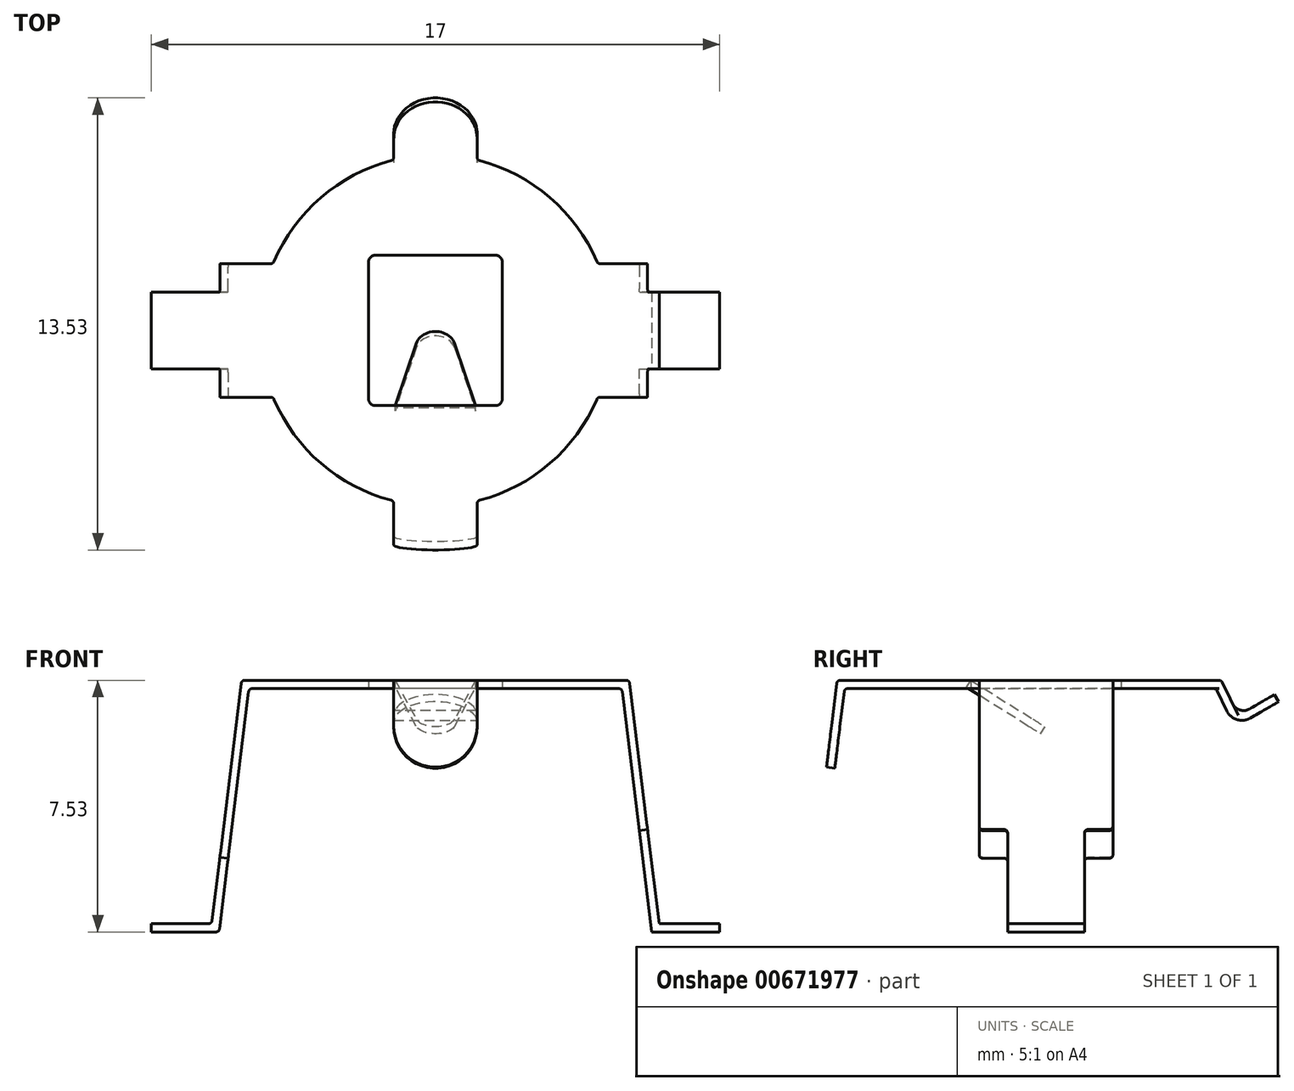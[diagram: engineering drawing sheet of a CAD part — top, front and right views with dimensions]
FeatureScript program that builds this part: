
annotation { "Feature Type Name" : "Feature", "Feature Type Description" : "" }
export const myFeature = defineFeature(function(context is Context, id is Id, definition is map)
    precondition{}
    {
        {
            var Q0;
            Q0=qCreatedBy(makeId("Top.planeOp"),FACE);
            var sketch = newSketch(context, id + "F0", { "sketchPlane" : qUnion([Q0])});
            skArc(sketch, "E0", {"start": v(-1.25, 5.1) * mm, "mid": v(-3.42, 3.98) * mm, "end": v(-4.85, 2) * mm});
            skLineSegment(sketch, "E1", {"start": v(-1.25, 5.24) * mm, "end": v(-1.25, 5.1) * mm});
            skLineSegment(sketch, "E2", {"start": v(1.25, 5.1) * mm, "end": v(1.25, 5.24) * mm});
            skLineSegment(sketch, "E3", {"start": v(-1.25, -5.1) * mm, "end": v(-1.25, -6.25) * mm});
            skLineSegment(sketch, "E4", {"start": v(-1.25, -6.25) * mm, "end": v(1.25, -6.25) * mm});
            skLineSegment(sketch, "E5", {"start": v(1.25, -6.25) * mm, "end": v(1.25, -5.1) * mm});
            skArc(sketch, "E6.trimOffspring", {"start": v(1.25, -5.1) * mm, "mid": v(3.42, -3.98) * mm, "end": v(4.85, -2) * mm});
            skPoint(sketch, "E7.end.orphan", {"position": v(0, -6.25) * mm});
            skArc(sketch, "E8.trimOffspring", {"start": v(-4.85, -2) * mm, "mid": v(-3.42, -3.98) * mm, "end": v(-1.25, -5.1) * mm});
            skArc(sketch, "E9.trimOffspring", {"start": v(4.85, 2) * mm, "mid": v(3.42, 3.98) * mm, "end": v(1.25, 5.1) * mm});
            skLineSegment(sketch, "E10", {"start": v(-5.8, 2) * mm, "end": v(-4.85, 2) * mm});
            skLineSegment(sketch, "E11", {"start": v(-5.8, 2) * mm, "end": v(-5.8, -2) * mm});
            skLineSegment(sketch, "E12", {"start": v(-5.8, -2) * mm, "end": v(-4.85, -2) * mm});
            skLineSegment(sketch, "E13", {"start": v(5.8, 2) * mm, "end": v(4.85, 2) * mm});
            skLineSegment(sketch, "E14", {"start": v(5.8, -2) * mm, "end": v(4.85, -2) * mm});
            skLineSegment(sketch, "E15", {"start": v(5.8, -2) * mm, "end": v(5.8, 2) * mm});
            skLineSegment(sketch, "E16", {"start": v(-1.25, 5.24) * mm, "end": v(1.25, 5.24) * mm});
            skLineSegment(sketch, "E17.bottom", {"start": v(2, -2.25) * mm, "end": v(-2, -2.25) * mm});
            skLineSegment(sketch, "E17.top", {"start": v(2, 2.25) * mm, "end": v(-2, 2.25) * mm});
            skLineSegment(sketch, "E17.left", {"start": v(2, -2.25) * mm, "end": v(2, 2.25) * mm});
            skLineSegment(sketch, "E17.right", {"start": v(-2, -2.25) * mm, "end": v(-2, 2.25) * mm});
            skSolve(sketch);
        }
        {
            var Q0;
            Q0 = qSketchRegion(id + "F0", true);
            extrude(context, id + "F1", {"entities" : qUnion([Q0]), "depth" : 0.25 * mm, "offsetDistance" : 25 * mm});
        }
        {
            var Q0;
            Q0=makeQuery(id+"F1.opExtrude","SWEPT_FACE",FACE,{"disambiguationData":[OSD([sQuery(id+"F0.wireOp",EDGE,"E12")])]});
            var sketch = newSketch(context, id + "F2", { "sketchPlane" : qUnion([Q0])});
            skLineSegment(sketch, "E18", {"start": v(-5.8, 0.25) * mm, "end": v(-6.7, -7.03) * mm});
            skLineSegment(sketch, "E19", {"start": v(-5.8, 0.25) * mm, "end": v(-5.55, 0.22) * mm});
            skLineSegment(sketch, "E20", {"start": v(-5.55, 0.22) * mm, "end": v(-6.47, -7.28) * mm});
            skLineSegment(sketch, "E21", {"start": v(-6.47, -7.28) * mm, "end": v(-8.5, -7.28) * mm});
            skLineSegment(sketch, "E22", {"start": v(-8.5, -7.28) * mm, "end": v(-8.5, -7.03) * mm});
            skLineSegment(sketch, "E23", {"start": v(-8.5, -7.03) * mm, "end": v(-6.7, -7.03) * mm});
            skLineSegment(sketch, "E24.MirrorCS", {"start": v(8.5, -7.28) * mm, "end": v(8.5, -7.03) * mm});
            skLineSegment(sketch, "E25.MirrorCS", {"start": v(5.8, 0.25) * mm, "end": v(5.55, 0.22) * mm});
            skLineSegment(sketch, "E26.MirrorCS", {"start": v(5.55, 0.22) * mm, "end": v(6.47, -7.28) * mm});
            skLineSegment(sketch, "E27.MirrorCS", {"start": v(5.8, 0.25) * mm, "end": v(6.7, -7.03) * mm});
            skLineSegment(sketch, "E28.MirrorCS", {"start": v(8.5, -7.03) * mm, "end": v(6.7, -7.03) * mm});
            skLineSegment(sketch, "E29.MirrorCS", {"start": v(6.47, -7.28) * mm, "end": v(8.5, -7.28) * mm});
            skSolve(sketch);
        }
        {
            var Q0;
            Q0 = qSketchRegion(id + "F2", true);
            extrude(context, id + "F3", {"entities" : qUnion([Q0]), "operationType" : NewBodyOperationType.ADD, "oppositeDirection" : true, "depth" : 4 * mm, "offsetDistance" : 25 * mm});
        }
        {
            var Q0;
            Q0=makeQuery(id+"F3.opExtrude","SWEPT_FACE",FACE,{"disambiguationData":[OSD([sQuery(id+"F2.wireOp",EDGE,"E18")])]});
            var sketch = newSketch(context, id + "F4", { "sketchPlane" : qUnion([Q0])});
            skLineSegment(sketch, "E30.bottom", {"start": v(-2, -5.8) * mm, "end": v(-1.15, -5.8) * mm});
            skLineSegment(sketch, "E30.top", {"start": v(-2, -7.8) * mm, "end": v(-1.15, -7.8) * mm});
            skLineSegment(sketch, "E30.left", {"start": v(-2, -5.8) * mm, "end": v(-2, -7.8) * mm});
            skLineSegment(sketch, "E30.right", {"start": v(-1.15, -5.8) * mm, "end": v(-1.15, -7.8) * mm});
            skLineSegment(sketch, "E31.bottom", {"start": v(2, -5.8) * mm, "end": v(1.15, -5.8) * mm});
            skLineSegment(sketch, "E31.top", {"start": v(2, -7.8) * mm, "end": v(1.15, -7.8) * mm});
            skLineSegment(sketch, "E31.left", {"start": v(2, -5.8) * mm, "end": v(2, -7.8) * mm});
            skLineSegment(sketch, "E31.right", {"start": v(1.15, -5.8) * mm, "end": v(1.15, -7.8) * mm});
            skSolve(sketch);
        }
        {
            var Q0;
            Q0 = qSketchRegion(id + "F4", true);
            extrude(context, id + "F5", {"entities" : qUnion([Q0]), "operationType" : NewBodyOperationType.REMOVE, "endBound" : BoundingType.UP_TO_NEXT, "oppositeDirection" : true, "depth" : 25 * mm, "offsetDistance" : 25 * mm});
        }
        {
            var Q0;
            Q0=makeQuery(id+"F3.opExtrude","SWEPT_FACE",FACE,{"disambiguationData":[OSD([sQuery(id+"F2.wireOp",EDGE,"E23")])]});
            var sketch = newSketch(context, id + "F6", { "sketchPlane" : qUnion([Q0])});
            skLineSegment(sketch, "E32.bottom", {"start": v(-6.7, 1.15) * mm, "end": v(-8.5, 1.15) * mm});
            skLineSegment(sketch, "E32.top", {"start": v(-6.7, 2) * mm, "end": v(-8.5, 2) * mm});
            skLineSegment(sketch, "E32.left", {"start": v(-6.7, 1.15) * mm, "end": v(-6.7, 2) * mm});
            skLineSegment(sketch, "E32.right", {"start": v(-8.5, 1.15) * mm, "end": v(-8.5, 2) * mm});
            skLineSegment(sketch, "E33.bottom", {"start": v(-6.7, -1.15) * mm, "end": v(-8.5, -1.15) * mm});
            skLineSegment(sketch, "E33.top", {"start": v(-6.7, -2) * mm, "end": v(-8.5, -2) * mm});
            skLineSegment(sketch, "E33.left", {"start": v(-6.7, -1.15) * mm, "end": v(-6.7, -2) * mm});
            skLineSegment(sketch, "E33.right", {"start": v(-8.5, -1.15) * mm, "end": v(-8.5, -2) * mm});
            skSolve(sketch);
        }
        {
            var Q0;
            Q0 = qSketchRegion(id + "F6", true);
            extrude(context, id + "F7", {"entities" : qUnion([Q0]), "operationType" : NewBodyOperationType.REMOVE, "endBound" : BoundingType.UP_TO_NEXT, "oppositeDirection" : true, "depth" : 25 * mm, "offsetDistance" : 25 * mm});
        }
        {
            var Q0;
            Q0=makeQuery(id+"F7.boolean.opBoolean","COPY",FACE,{"derivedFrom":makeQuery(id+"F7.opExtrude","SWEPT_FACE",FACE,{"disambiguationData":[OSD([sQuery(id+"F6.wireOp",EDGE,"E32.left")])]})});
            var sketch = newSketch(context, id + "F8", { "sketchPlane" : qUnion([Q0])});
            skLineSegment(sketch, "E34.bottom", {"start": v(-2, -7.03) * mm, "end": v(-1.15, -7.03) * mm});
            skLineSegment(sketch, "E34.top", {"start": v(-2, -7.28) * mm, "end": v(-1.15, -7.28) * mm});
            skLineSegment(sketch, "E34.left", {"start": v(-2, -7.03) * mm, "end": v(-2, -7.28) * mm});
            skLineSegment(sketch, "E34.right", {"start": v(-1.15, -7.03) * mm, "end": v(-1.15, -7.28) * mm});
            skSolve(sketch);
        }
        {
            var Q0;
            Q0 = qSketchRegion(id + "F8", true);
            extrude(context, id + "F9", {"entities" : qUnion([Q0]), "operationType" : NewBodyOperationType.REMOVE, "endBound" : BoundingType.UP_TO_NEXT, "oppositeDirection" : true, "depth" : 25 * mm, "offsetDistance" : 25 * mm});
        }
        {
            var Q0;
            Q0=makeQuery(id+"F7.boolean.opBoolean","COPY",FACE,{"derivedFrom":makeQuery(id+"F7.opExtrude","SWEPT_FACE",FACE,{"disambiguationData":[OSD([sQuery(id+"F6.wireOp",EDGE,"E33.left")])]})});
            var sketch = newSketch(context, id + "F10", { "sketchPlane" : qUnion([Q0])});
            skLineSegment(sketch, "E35.bottom", {"start": v(1.15, -7.03) * mm, "end": v(2, -7.03) * mm});
            skLineSegment(sketch, "E35.top", {"start": v(1.15, -7.28) * mm, "end": v(2, -7.28) * mm});
            skLineSegment(sketch, "E35.left", {"start": v(1.15, -7.03) * mm, "end": v(1.15, -7.28) * mm});
            skLineSegment(sketch, "E35.right", {"start": v(2, -7.03) * mm, "end": v(2, -7.28) * mm});
            skSolve(sketch);
        }
        {
            var Q0;
            Q0 = qSketchRegion(id + "F10", true);
            extrude(context, id + "F11", {"entities" : qUnion([Q0]), "operationType" : NewBodyOperationType.REMOVE, "endBound" : BoundingType.UP_TO_NEXT, "oppositeDirection" : true, "depth" : 25 * mm, "offsetDistance" : 25 * mm});
        }
        {
            var Q0;
            Q0=makeQuery(id+"F3.opExtrude","SWEPT_FACE",FACE,{"disambiguationData":[OSD([sQuery(id+"F2.wireOp",EDGE,"E27.MirrorCS")])]});
            var sketch = newSketch(context, id + "F12", { "sketchPlane" : qUnion([Q0])});
            skLineSegment(sketch, "E36.bottom", {"start": v(-2, -4.96) * mm, "end": v(-1.15, -4.96) * mm});
            skLineSegment(sketch, "E36.top", {"start": v(-2, -7.8) * mm, "end": v(-1.15, -7.8) * mm});
            skLineSegment(sketch, "E36.left", {"start": v(-2, -4.96) * mm, "end": v(-2, -7.8) * mm});
            skLineSegment(sketch, "E36.right", {"start": v(-1.15, -4.96) * mm, "end": v(-1.15, -7.8) * mm});
            skLineSegment(sketch, "E37.bottom", {"start": v(2, -7.8) * mm, "end": v(1.15, -7.8) * mm});
            skLineSegment(sketch, "E37.top", {"start": v(2, -4.96) * mm, "end": v(1.15, -4.96) * mm});
            skLineSegment(sketch, "E37.left", {"start": v(2, -7.8) * mm, "end": v(2, -4.96) * mm});
            skLineSegment(sketch, "E37.right", {"start": v(1.15, -7.8) * mm, "end": v(1.15, -4.96) * mm});
            skSolve(sketch);
        }
        {
            var Q0;
            Q0 = qSketchRegion(id + "F12", true);
            extrude(context, id + "F13", {"entities" : qUnion([Q0]), "operationType" : NewBodyOperationType.REMOVE, "endBound" : BoundingType.UP_TO_NEXT, "oppositeDirection" : true, "depth" : 25 * mm, "offsetDistance" : 25 * mm});
        }
        {
            var Q0;
            Q0=makeQuery(id+"F3.opExtrude","SWEPT_FACE",FACE,{"disambiguationData":[OSD([sQuery(id+"F2.wireOp",EDGE,"E28.MirrorCS")])]});
            var sketch = newSketch(context, id + "F14", { "sketchPlane" : qUnion([Q0])});
            skLineSegment(sketch, "E38.bottom", {"start": v(6.7, -2) * mm, "end": v(8.5, -2) * mm});
            skLineSegment(sketch, "E38.top", {"start": v(6.7, -1.15) * mm, "end": v(8.5, -1.15) * mm});
            skLineSegment(sketch, "E38.left", {"start": v(6.7, -2) * mm, "end": v(6.7, -1.15) * mm});
            skLineSegment(sketch, "E38.right", {"start": v(8.5, -2) * mm, "end": v(8.5, -1.15) * mm});
            skLineSegment(sketch, "E39.bottom", {"start": v(6.7, 1.15) * mm, "end": v(8.5, 1.15) * mm});
            skLineSegment(sketch, "E39.top", {"start": v(6.7, 2) * mm, "end": v(8.5, 2) * mm});
            skLineSegment(sketch, "E39.left", {"start": v(6.7, 1.15) * mm, "end": v(6.7, 2) * mm});
            skLineSegment(sketch, "E39.right", {"start": v(8.5, 1.15) * mm, "end": v(8.5, 2) * mm});
            skSolve(sketch);
        }
        {
            var Q0;
            Q0 = qSketchRegion(id + "F14", true);
            extrude(context, id + "F15", {"entities" : qUnion([Q0]), "operationType" : NewBodyOperationType.REMOVE, "endBound" : BoundingType.UP_TO_NEXT, "oppositeDirection" : true, "depth" : 25 * mm, "offsetDistance" : 25 * mm});
        }
        {
            var Q0;
            Q0=makeQuery(id+"F15.boolean.opBoolean","COPY",FACE,{"derivedFrom":makeQuery(id+"F15.opExtrude","SWEPT_FACE",FACE,{"disambiguationData":[OSD([sQuery(id+"F14.wireOp",EDGE,"E38.left")])]})});
            var sketch = newSketch(context, id + "F16", { "sketchPlane" : qUnion([Q0])});
            skLineSegment(sketch, "E40.bottom", {"start": v(-2, -7.03) * mm, "end": v(-1.15, -7.03) * mm});
            skLineSegment(sketch, "E40.top", {"start": v(-2, -7.28) * mm, "end": v(-1.15, -7.28) * mm});
            skLineSegment(sketch, "E40.left", {"start": v(-2, -7.03) * mm, "end": v(-2, -7.28) * mm});
            skLineSegment(sketch, "E40.right", {"start": v(-1.15, -7.03) * mm, "end": v(-1.15, -7.28) * mm});
            skSolve(sketch);
        }
        {
            var Q0;
            Q0 = qSketchRegion(id + "F16", true);
            extrude(context, id + "F17", {"entities" : qUnion([Q0]), "operationType" : NewBodyOperationType.REMOVE, "endBound" : BoundingType.UP_TO_NEXT, "oppositeDirection" : true, "depth" : 25 * mm, "offsetDistance" : 25 * mm});
        }
        {
            var Q0;
            Q0=makeQuery(id+"F15.boolean.opBoolean","COPY",FACE,{"derivedFrom":makeQuery(id+"F15.opExtrude","SWEPT_FACE",FACE,{"disambiguationData":[OSD([sQuery(id+"F14.wireOp",EDGE,"E39.left")])]})});
            var sketch = newSketch(context, id + "F18", { "sketchPlane" : qUnion([Q0])});
            skLineSegment(sketch, "E41.bottom", {"start": v(1.15, -7.03) * mm, "end": v(2, -7.03) * mm});
            skLineSegment(sketch, "E41.top", {"start": v(1.15, -7.28) * mm, "end": v(2, -7.28) * mm});
            skLineSegment(sketch, "E41.left", {"start": v(1.15, -7.03) * mm, "end": v(1.15, -7.28) * mm});
            skLineSegment(sketch, "E41.right", {"start": v(2, -7.03) * mm, "end": v(2, -7.28) * mm});
            skSolve(sketch);
        }
        {
            var Q0;
            Q0 = qSketchRegion(id + "F18", true);
            extrude(context, id + "F19", {"entities" : qUnion([Q0]), "operationType" : NewBodyOperationType.REMOVE, "endBound" : BoundingType.UP_TO_NEXT, "oppositeDirection" : true, "depth" : 25 * mm, "offsetDistance" : 25 * mm});
        }
        {
            var Q0;
            Q0=makeQuery(id+"F1.opExtrude","SWEPT_FACE",FACE,{"disambiguationData":[OSD([sQuery(id+"F0.wireOp",EDGE,"E3")])]});
            var sketch = newSketch(context, id + "F20", { "sketchPlane" : qUnion([Q0])});
            skLineSegment(sketch, "E42", {"start": v(6.25, 0.25) * mm, "end": v(6.57, -2.35) * mm});
            skLineSegment(sketch, "E43", {"start": v(6.57, -2.35) * mm, "end": v(6.32, -2.38) * mm});
            skLineSegment(sketch, "E44", {"start": v(6.25, 0.25) * mm, "end": v(6, 0.22) * mm});
            skLineSegment(sketch, "E45", {"start": v(6, 0.22) * mm, "end": v(6.32, -2.38) * mm});
            skSolve(sketch);
        }
        {
            var Q0;
            Q0 = qSketchRegion(id + "F20", true);
            extrude(context, id + "F21", {"entities" : qUnion([Q0]), "operationType" : NewBodyOperationType.ADD, "oppositeDirection" : true, "depth" : 2.5 * mm, "offsetDistance" : 25 * mm});
        }
        {
            var Q0;
            Q0=makeQuery(id+"F21.opExtrude","CAP_EDGE",EDGE,{"disambiguationData":[OSD([sQuery(id+"F20.wireOp",EDGE,"E43")])],"isStart":true});
            var Q1;
            Q1=makeQuery(id+"F21.opExtrude","CAP_EDGE",EDGE,{"disambiguationData":[OSD([sQuery(id+"F20.wireOp",EDGE,"E43")])],"isStart":false});
            fillet(context, id + "F22", {"entities" : qUnion([Q0, Q1]), "radius" : 1.25 * mm, "tangentPropagation" : true, "allowEdgeOverflow" : false});
        }
        {
            var Q0;
            Q0=makeQuery(id+"F1.opExtrude","SWEPT_FACE",FACE,{"disambiguationData":[OSD([sQuery(id+"F0.wireOp",EDGE,"E1")])]});
            var sketch = newSketch(context, id + "F23", { "sketchPlane" : qUnion([Q0])});
            skLineSegment(sketch, "E46", {"start": v(-5.24, 0.25) * mm, "end": v(-5.75, -0.8) * mm});
            skLineSegment(sketch, "E47", {"start": v(-5.24, 0.25) * mm, "end": v(-5.02, 0.14) * mm});
            skLineSegment(sketch, "E48", {"start": v(-5.64, -1.15) * mm, "end": v(-5.02, 0.14) * mm});
            skLineSegment(sketch, "E49", {"start": v(-5.64, -1.15) * mm, "end": v(-6.25, -0.8) * mm});
            skLineSegment(sketch, "E50", {"start": v(-6.25, -0.8) * mm, "end": v(-6.13, -0.58) * mm});
            skLineSegment(sketch, "E51", {"start": v(-6.13, -0.58) * mm, "end": v(-5.75, -0.8) * mm});
            skSolve(sketch);
        }
        {
            var Q0;
            Q0 = qSketchRegion(id + "F23", true);
            extrude(context, id + "F24", {"entities" : qUnion([Q0]), "operationType" : NewBodyOperationType.ADD, "oppositeDirection" : true, "depth" : 2.5 * mm, "offsetDistance" : 25 * mm});
        }
        {
            var Q0;
            Q0=makeQuery(id+"F24.opExtrude","SWEPT_EDGE",EDGE,{"disambiguationData":[OSD([sQuery(id+"F23.wireOp",EDGE,"E48"),sQuery(id+"F23.wireOp",EDGE,"E49")])]});
            fillet(context, id + "F25", {"entities" : qUnion([Q0]), "radius" : 0.5 * mm, "tangentPropagation" : true, "allowEdgeOverflow" : false});
        }
        {
            var Q0;
            Q0=makeQuery(id+"F24.opExtrude","SWEPT_FACE",FACE,{"disambiguationData":[OSD([sQuery(id+"F23.wireOp",EDGE,"E51")])]});
            var sketch = newSketch(context, id + "F26", { "sketchPlane" : qUnion([Q0])});
            skArc(sketch, "E52", {"start": v(1.25, 4.58) * mm, "mid": v(0, 5.83) * mm, "end": v(-1.25, 4.58) * mm});
            skSolve(sketch);
        }
        {
            var Q0;
            {var subQ0=sQuery(id+"F26.wireOp",EDGE,"E52");var subQ1=makeQuery(id+"F24.opExtrude","SWEPT_EDGE",EDGE,{"disambiguationData":[OSD([sQuery(id+"F23.wireOp",EDGE,"E50"),sQuery(id+"F23.wireOp",EDGE,"E51")])]});var subQ2=makeQuery(id+"F26.imprint","INTERSECT",VERTEX,{"disambiguationData":[OD(0.0)],"derivedFrom":[subQ1,subQ0]});Q0=makeQuery(id+"F26.imprint","IMPRINT",FACE,{"disambiguationData":[TD([[makeQuery(id+"F26.imprint","IMPRINT",EDGE,{"disambiguationData":[TD([[subQ2,-1.0]])],"derivedFrom":subQ0}),1.0]])]});}
            extrude(context, id + "F27", {"entities" : qUnion([Q0]), "operationType" : NewBodyOperationType.ADD, "oppositeDirection" : true, "depth" : 0.25 * mm, "offsetDistance" : 25 * mm});
        }
        {
            var Q0;
            {var subQ0=sQuery(id+"F23.wireOp",EDGE,"E51");Q0=makeQuery(id+"F27.boolean.opBoolean","MERGE",FACE,{"derivedFrom":[makeQuery(id+"F24.opExtrude","SWEPT_FACE",FACE,{"disambiguationData":[OSD([subQ0])]}),makeQuery(id+"F27.opExtrude","CAP_FACE",FACE,{"disambiguationData":[OSD([sQuery(id+"F23.wireOp",EDGE,"E50"),subQ0,sQuery(id+"F26.wireOp",EDGE,"E52")])],"isStart":true})]});}
            var sketch = newSketch(context, id + "F28", { "sketchPlane" : qUnion([Q0])});
            skArc(sketch, "E53", {"start": v(1.25, 4.58) * mm, "mid": v(0, 5.83) * mm, "end": v(-1.25, 4.58) * mm});
            skSolve(sketch);
        }
        {
            var Q0;
            {var subQ1=sQuery(id+"F23.wireOp",EDGE,"E51");var subQ2=makeQuery(id+"F24.opExtrude","CAP_EDGE",EDGE,{"disambiguationData":[OSD([subQ1])],"isStart":true});Q0=makeQuery(id+"F28.imprint","IMPRINT",FACE,{"disambiguationData":[TD([[makeQuery(id+"F28.imprint","IMPRINT",EDGE,{"derivedFrom":subQ2}),1.0]])]});}
            var Q1;
            {var subQ1=sQuery(id+"F23.wireOp",EDGE,"E51");var subQ2=makeQuery(id+"F24.opExtrude","CAP_EDGE",EDGE,{"disambiguationData":[OSD([subQ1])],"isStart":false});Q1=makeQuery(id+"F28.imprint","IMPRINT",FACE,{"disambiguationData":[TD([[makeQuery(id+"F28.imprint","IMPRINT",EDGE,{"derivedFrom":subQ2}),-1.0]])]});}
            extrude(context, id + "F29", {"entities" : qUnion([Q0, Q1]), "operationType" : NewBodyOperationType.REMOVE, "endBound" : BoundingType.UP_TO_NEXT, "oppositeDirection" : true, "depth" : 25 * mm, "offsetDistance" : 25 * mm});
        }
        {
            var Q0;
            Q0=makeQuery(id+"F24.opExtrude","SWEPT_EDGE",EDGE,{"disambiguationData":[OSD([sQuery(id+"F23.wireOp",EDGE,"E46"),sQuery(id+"F23.wireOp",EDGE,"E51")])]});
            fillet(context, id + "F30", {"entities" : qUnion([Q0]), "radius" : 0.35 * mm, "tangentPropagation" : true, "allowEdgeOverflow" : false});
        }
        {
            var Q0;
            Q0=qCreatedBy(makeId("Right.planeOp"),FACE);
            var sketch = newSketch(context, id + "F31", { "sketchPlane" : qUnion([Q0])});
            skLineSegment(sketch, "E54", {"start": v(-2.25, 0.25) * mm, "end": v(-0.03, -1.14) * mm});
            skLineSegment(sketch, "E55", {"start": v(-2.25, 0.25) * mm, "end": v(-2.38, 0.04) * mm});
            skLineSegment(sketch, "E56", {"start": v(-0.03, -1.14) * mm, "end": v(-0.16, -1.35) * mm});
            skLineSegment(sketch, "E57", {"start": v(-2.38, 0.04) * mm, "end": v(-0.16, -1.35) * mm});
            skSolve(sketch);
        }
        {
            var Q0;
            Q0 = qSketchRegion(id + "F31", true);
            extrude(context, id + "F32", {"entities" : qUnion([Q0]), "operationType" : NewBodyOperationType.ADD, "depth" : 1.2 * mm, "offsetDistance" : 25 * mm, "hasSecondDirection" : true, "secondDirectionOppositeDirection" : true, "secondDirectionDepth" : 1.2 * mm});
        }
        {
            var Q0;
            Q0=makeQuery(id+"F32.opExtrude","SWEPT_FACE",FACE,{"disambiguationData":[OSD([sQuery(id+"F31.wireOp",EDGE,"E54")])]});
            var sketch = newSketch(context, id + "F33", { "sketchPlane" : qUnion([Q0])});
            skArc(sketch, "E58", {"start": v(0.58, 0.14) * mm, "mid": v(0, 0.58) * mm, "end": v(-0.58, 0.14) * mm});
            skLineSegment(sketch, "E59", {"start": v(1.2, -2.04) * mm, "end": v(0.58, 0.14) * mm});
            skLineSegment(sketch, "E60", {"start": v(-1.2, -2.04) * mm, "end": v(-0.58, 0.14) * mm});
            skSolve(sketch);
        }
        {
            var Q0;
            Q0 = qSketchRegion(id + "F33", true);
            var Q1;
            {var subQ0=sQuery(id+"F33.wireOp",EDGE,"E59");Q1=makeQuery(id+"F33.imprint","IMPRINT",FACE,{"disambiguationData":[TD([[makeQuery(id+"F33.imprint","IMPRINT",EDGE,{"derivedFrom":subQ0}),-1.0]])]});}
            var Q2;
            {var subQ0=sQuery(id+"F33.wireOp",EDGE,"E60");Q2=makeQuery(id+"F33.imprint","IMPRINT",FACE,{"disambiguationData":[TD([[makeQuery(id+"F33.imprint","IMPRINT",EDGE,{"derivedFrom":subQ0}),1.0]])]});}
            extrude(context, id + "F34", {"entities" : qUnion([Q0, Q1, Q2]), "operationType" : NewBodyOperationType.REMOVE, "endBound" : BoundingType.UP_TO_NEXT, "oppositeDirection" : true, "depth" : 25 * mm, "offsetDistance" : 25 * mm});
        }
        {
            var Q0;
            Q0=makeQuery(id+"F1.opExtrude","SWEPT_EDGE",EDGE,{"disambiguationData":[OSD([sQuery(id+"F0.wireOp",EDGE,"E17.bottom"),sQuery(id+"F0.wireOp",EDGE,"E17.left")])]});
            var Q1;
            Q1=makeQuery(id+"F1.opExtrude","SWEPT_EDGE",EDGE,{"disambiguationData":[OSD([sQuery(id+"F0.wireOp",EDGE,"E17.bottom"),sQuery(id+"F0.wireOp",EDGE,"E17.right")])]});
            var Q2;
            Q2=makeQuery(id+"F1.opExtrude","SWEPT_EDGE",EDGE,{"disambiguationData":[OSD([sQuery(id+"F0.wireOp",EDGE,"E17.top"),sQuery(id+"F0.wireOp",EDGE,"E17.left")])]});
            var Q3;
            Q3=makeQuery(id+"F1.opExtrude","SWEPT_EDGE",EDGE,{"disambiguationData":[OSD([sQuery(id+"F0.wireOp",EDGE,"E17.top"),sQuery(id+"F0.wireOp",EDGE,"E17.right")])]});
            fillet(context, id + "F35", {"entities" : qUnion([Q0, Q1, Q2, Q3]), "radius" : 0.2 * mm, "tangentPropagation" : true, "allowEdgeOverflow" : false});
        }
        {
            var Q0;
            Q0=makeQuery(id+"F5.boolean.opBoolean","SPLIT",EDGE,{"derivedFrom":makeQuery(id+"F3.opExtrude","SWEPT_EDGE",EDGE,{"disambiguationData":[OSD([sQuery(id+"F2.wireOp",EDGE,"E18"),sQuery(id+"F2.wireOp",EDGE,"E23")])]})});
            var Q1;
            Q1=makeQuery(id+"F3.opExtrude","SWEPT_EDGE",EDGE,{"disambiguationData":[OSD([sQuery(id+"F2.wireOp",EDGE,"E20"),sQuery(id+"F2.wireOp",EDGE,"E21")])]});
            var Q2;
            {var subQ0=sQuery(id+"F0.wireOp",EDGE,"E11");Q2=makeQuery(id+"F3.boolean.opBoolean","MERGE",EDGE,{"derivedFrom":[makeQuery(id+"F1.opExtrude","CAP_EDGE",EDGE,{"disambiguationData":[OSD([subQ0])],"isStart":false}),makeQuery(id+"F3.opExtrude","SWEPT_EDGE",EDGE,{"disambiguationData":[OSD([subQ0,sQuery(id+"F0.wireOp",EDGE,"E12"),sQuery(id+"F2.wireOp",EDGE,"E18"),sQuery(id+"F2.wireOp",EDGE,"E19")])]})]});}
            var Q3;
            Q3=makeQuery(id+"F3.boolean.opBoolean","INTERSECT",EDGE,{"derivedFrom":[makeQuery(id+"F1.opExtrude","CAP_FACE",FACE,{"disambiguationData":[OSD([sQuery(id+"F0.wireOp",EDGE,"E0"),sQuery(id+"F0.wireOp",EDGE,"E1"),sQuery(id+"F0.wireOp",EDGE,"E2"),sQuery(id+"F0.wireOp",EDGE,"E3"),sQuery(id+"F0.wireOp",EDGE,"E4"),sQuery(id+"F0.wireOp",EDGE,"E5"),sQuery(id+"F0.wireOp",EDGE,"E6.trimOffspring"),sQuery(id+"F0.wireOp",EDGE,"E8.trimOffspring"),sQuery(id+"F0.wireOp",EDGE,"E9.trimOffspring"),sQuery(id+"F0.wireOp",EDGE,"E10"),sQuery(id+"F0.wireOp",EDGE,"E11"),sQuery(id+"F0.wireOp",EDGE,"E12"),sQuery(id+"F0.wireOp",EDGE,"E13"),sQuery(id+"F0.wireOp",EDGE,"E14"),sQuery(id+"F0.wireOp",EDGE,"E15"),sQuery(id+"F0.wireOp",EDGE,"E16"),sQuery(id+"F0.wireOp",EDGE,"E17.bottom"),sQuery(id+"F0.wireOp",EDGE,"E17.top"),sQuery(id+"F0.wireOp",EDGE,"E17.left"),sQuery(id+"F0.wireOp",EDGE,"E17.right")])],"isStart":true}),makeQuery(id+"F3.opExtrude","SWEPT_FACE",FACE,{"disambiguationData":[OSD([sQuery(id+"F2.wireOp",EDGE,"E20")])]})]});
            var Q4;
            {var subQ0=sQuery(id+"F0.wireOp",EDGE,"E16");Q4=makeQuery(id+"F24.boolean.opBoolean","MERGE",EDGE,{"derivedFrom":[makeQuery(id+"F1.opExtrude","CAP_EDGE",EDGE,{"disambiguationData":[OSD([subQ0])],"isStart":false}),makeQuery(id+"F24.opExtrude","SWEPT_EDGE",EDGE,{"disambiguationData":[OSD([sQuery(id+"F0.wireOp",EDGE,"E1"),subQ0,sQuery(id+"F23.wireOp",EDGE,"E46"),sQuery(id+"F23.wireOp",EDGE,"E47")])]})]});}
            var Q5;
            Q5=makeQuery(id+"F3.boolean.opBoolean","MERGE",EDGE,{"derivedFrom":[makeQuery(id+"F1.opExtrude","CAP_EDGE",EDGE,{"disambiguationData":[OSD([sQuery(id+"F0.wireOp",EDGE,"E15")])],"isStart":false}),makeQuery(id+"F3.opExtrude","SWEPT_EDGE",EDGE,{"disambiguationData":[OSD([sQuery(id+"F2.wireOp",EDGE,"E25.MirrorCS"),sQuery(id+"F2.wireOp",EDGE,"E27.MirrorCS")])]})]});
            var Q6;
            {var subQ0=sQuery(id+"F0.wireOp",EDGE,"E4");Q6=makeQuery(id+"F21.boolean.opBoolean","MERGE",EDGE,{"derivedFrom":[makeQuery(id+"F1.opExtrude","CAP_EDGE",EDGE,{"disambiguationData":[OSD([subQ0])],"isStart":false}),makeQuery(id+"F21.opExtrude","SWEPT_EDGE",EDGE,{"disambiguationData":[OSD([sQuery(id+"F0.wireOp",EDGE,"E3"),subQ0,sQuery(id+"F20.wireOp",EDGE,"E42"),sQuery(id+"F20.wireOp",EDGE,"E44")])]})]});}
            var Q7;
            Q7=makeQuery(id+"F24.boolean.opBoolean","INTERSECT",EDGE,{"derivedFrom":[makeQuery(id+"F1.opExtrude","CAP_FACE",FACE,{"disambiguationData":[OSD([sQuery(id+"F0.wireOp",EDGE,"E0"),sQuery(id+"F0.wireOp",EDGE,"E1"),sQuery(id+"F0.wireOp",EDGE,"E2"),sQuery(id+"F0.wireOp",EDGE,"E3"),sQuery(id+"F0.wireOp",EDGE,"E4"),sQuery(id+"F0.wireOp",EDGE,"E5"),sQuery(id+"F0.wireOp",EDGE,"E6.trimOffspring"),sQuery(id+"F0.wireOp",EDGE,"E8.trimOffspring"),sQuery(id+"F0.wireOp",EDGE,"E9.trimOffspring"),sQuery(id+"F0.wireOp",EDGE,"E10"),sQuery(id+"F0.wireOp",EDGE,"E11"),sQuery(id+"F0.wireOp",EDGE,"E12"),sQuery(id+"F0.wireOp",EDGE,"E13"),sQuery(id+"F0.wireOp",EDGE,"E14"),sQuery(id+"F0.wireOp",EDGE,"E15"),sQuery(id+"F0.wireOp",EDGE,"E16"),sQuery(id+"F0.wireOp",EDGE,"E17.bottom"),sQuery(id+"F0.wireOp",EDGE,"E17.top"),sQuery(id+"F0.wireOp",EDGE,"E17.left"),sQuery(id+"F0.wireOp",EDGE,"E17.right")])],"isStart":true}),makeQuery(id+"F24.opExtrude","SWEPT_FACE",FACE,{"disambiguationData":[OSD([sQuery(id+"F23.wireOp",EDGE,"E48")])]})]});
            var Q8;
            Q8=makeQuery(id+"F21.boolean.opBoolean","INTERSECT",EDGE,{"derivedFrom":[makeQuery(id+"F1.opExtrude","CAP_FACE",FACE,{"disambiguationData":[OSD([sQuery(id+"F0.wireOp",EDGE,"E0"),sQuery(id+"F0.wireOp",EDGE,"E1"),sQuery(id+"F0.wireOp",EDGE,"E2"),sQuery(id+"F0.wireOp",EDGE,"E3"),sQuery(id+"F0.wireOp",EDGE,"E4"),sQuery(id+"F0.wireOp",EDGE,"E5"),sQuery(id+"F0.wireOp",EDGE,"E6.trimOffspring"),sQuery(id+"F0.wireOp",EDGE,"E8.trimOffspring"),sQuery(id+"F0.wireOp",EDGE,"E9.trimOffspring"),sQuery(id+"F0.wireOp",EDGE,"E10"),sQuery(id+"F0.wireOp",EDGE,"E11"),sQuery(id+"F0.wireOp",EDGE,"E12"),sQuery(id+"F0.wireOp",EDGE,"E13"),sQuery(id+"F0.wireOp",EDGE,"E14"),sQuery(id+"F0.wireOp",EDGE,"E15"),sQuery(id+"F0.wireOp",EDGE,"E16"),sQuery(id+"F0.wireOp",EDGE,"E17.bottom"),sQuery(id+"F0.wireOp",EDGE,"E17.top"),sQuery(id+"F0.wireOp",EDGE,"E17.left"),sQuery(id+"F0.wireOp",EDGE,"E17.right")])],"isStart":true}),makeQuery(id+"F21.opExtrude","SWEPT_FACE",FACE,{"disambiguationData":[OSD([sQuery(id+"F20.wireOp",EDGE,"E45")])]})]});
            var Q9;
            Q9=makeQuery(id+"F3.boolean.opBoolean","INTERSECT",EDGE,{"derivedFrom":[makeQuery(id+"F1.opExtrude","CAP_FACE",FACE,{"disambiguationData":[OSD([sQuery(id+"F0.wireOp",EDGE,"E0"),sQuery(id+"F0.wireOp",EDGE,"E1"),sQuery(id+"F0.wireOp",EDGE,"E2"),sQuery(id+"F0.wireOp",EDGE,"E3"),sQuery(id+"F0.wireOp",EDGE,"E4"),sQuery(id+"F0.wireOp",EDGE,"E5"),sQuery(id+"F0.wireOp",EDGE,"E6.trimOffspring"),sQuery(id+"F0.wireOp",EDGE,"E8.trimOffspring"),sQuery(id+"F0.wireOp",EDGE,"E9.trimOffspring"),sQuery(id+"F0.wireOp",EDGE,"E10"),sQuery(id+"F0.wireOp",EDGE,"E11"),sQuery(id+"F0.wireOp",EDGE,"E12"),sQuery(id+"F0.wireOp",EDGE,"E13"),sQuery(id+"F0.wireOp",EDGE,"E14"),sQuery(id+"F0.wireOp",EDGE,"E15"),sQuery(id+"F0.wireOp",EDGE,"E16"),sQuery(id+"F0.wireOp",EDGE,"E17.bottom"),sQuery(id+"F0.wireOp",EDGE,"E17.top"),sQuery(id+"F0.wireOp",EDGE,"E17.left"),sQuery(id+"F0.wireOp",EDGE,"E17.right")])],"isStart":true}),makeQuery(id+"F3.opExtrude","SWEPT_FACE",FACE,{"disambiguationData":[OSD([sQuery(id+"F2.wireOp",EDGE,"E26.MirrorCS")])]})]});
            var Q10;
            Q10=makeQuery(id+"F1.opExtrude","SWEPT_EDGE",EDGE,{"disambiguationData":[OSD([sQuery(id+"F0.wireOp",EDGE,"E5"),sQuery(id+"F0.wireOp",EDGE,"E6.trimOffspring")])]});
            var Q11;
            Q11=makeQuery(id+"F1.opExtrude","SWEPT_EDGE",EDGE,{"disambiguationData":[OSD([sQuery(id+"F0.wireOp",EDGE,"E6.trimOffspring"),sQuery(id+"F0.wireOp",EDGE,"E14")])]});
            var Q12;
            Q12=makeQuery(id+"F13.boolean.opBoolean","COPY",EDGE,{"derivedFrom":makeQuery(id+"F13.opExtrude","SWEPT_EDGE",EDGE,{"disambiguationData":[OSD([sQuery(id+"F2.wireOp",EDGE,"E27.MirrorCS"),sQuery(id+"F12.wireOp",EDGE,"E36.bottom"),sQuery(id+"F12.wireOp",EDGE,"E36.left")])]})});
            var Q13;
            Q13=makeQuery(id+"F13.boolean.opBoolean","COPY",EDGE,{"derivedFrom":makeQuery(id+"F13.opExtrude","SWEPT_EDGE",EDGE,{"disambiguationData":[OSD([sQuery(id+"F12.wireOp",EDGE,"E36.bottom"),sQuery(id+"F12.wireOp",EDGE,"E36.right")])]})});
            var Q14;
            Q14=makeQuery(id+"F15.boolean.opBoolean","COPY",EDGE,{"derivedFrom":makeQuery(id+"F15.opExtrude","SWEPT_EDGE",EDGE,{"disambiguationData":[OSD([sQuery(id+"F2.wireOp",EDGE,"E24.MirrorCS"),sQuery(id+"F2.wireOp",EDGE,"E28.MirrorCS"),sQuery(id+"F14.wireOp",EDGE,"E38.top"),sQuery(id+"F14.wireOp",EDGE,"E38.right")])]})});
            var Q15;
            Q15=makeQuery(id+"F15.boolean.opBoolean","COPY",EDGE,{"derivedFrom":makeQuery(id+"F15.opExtrude","SWEPT_EDGE",EDGE,{"disambiguationData":[OSD([sQuery(id+"F2.wireOp",EDGE,"E24.MirrorCS"),sQuery(id+"F2.wireOp",EDGE,"E28.MirrorCS"),sQuery(id+"F14.wireOp",EDGE,"E39.bottom"),sQuery(id+"F14.wireOp",EDGE,"E39.right")])]})});
            var Q16;
            Q16=makeQuery(id+"F13.boolean.opBoolean","COPY",EDGE,{"derivedFrom":makeQuery(id+"F13.opExtrude","SWEPT_EDGE",EDGE,{"disambiguationData":[OSD([sQuery(id+"F2.wireOp",EDGE,"E27.MirrorCS"),sQuery(id+"F12.wireOp",EDGE,"E37.top"),sQuery(id+"F12.wireOp",EDGE,"E37.left")])]})});
            var Q17;
            Q17=makeQuery(id+"F13.boolean.opBoolean","COPY",EDGE,{"derivedFrom":makeQuery(id+"F13.opExtrude","SWEPT_EDGE",EDGE,{"disambiguationData":[OSD([sQuery(id+"F12.wireOp",EDGE,"E37.top"),sQuery(id+"F12.wireOp",EDGE,"E37.right")])]})});
            var Q18;
            Q18=makeQuery(id+"F1.opExtrude","SWEPT_EDGE",EDGE,{"disambiguationData":[OSD([sQuery(id+"F0.wireOp",EDGE,"E9.trimOffspring"),sQuery(id+"F0.wireOp",EDGE,"E13")])]});
            var Q19;
            Q19=makeQuery(id+"F1.opExtrude","SWEPT_EDGE",EDGE,{"disambiguationData":[OSD([sQuery(id+"F0.wireOp",EDGE,"E0"),sQuery(id+"F0.wireOp",EDGE,"E1")])]});
            var Q20;
            Q20=makeQuery(id+"F1.opExtrude","SWEPT_EDGE",EDGE,{"disambiguationData":[OSD([sQuery(id+"F0.wireOp",EDGE,"E2"),sQuery(id+"F0.wireOp",EDGE,"E9.trimOffspring")])]});
            var Q21;
            Q21=makeQuery(id+"F1.opExtrude","SWEPT_EDGE",EDGE,{"disambiguationData":[OSD([sQuery(id+"F0.wireOp",EDGE,"E0"),sQuery(id+"F0.wireOp",EDGE,"E10")])]});
            var Q22;
            Q22=makeQuery(id+"F5.boolean.opBoolean","COPY",EDGE,{"derivedFrom":makeQuery(id+"F5.opExtrude","SWEPT_EDGE",EDGE,{"disambiguationData":[OSD([sQuery(id+"F4.wireOp",EDGE,"E30.bottom"),sQuery(id+"F4.wireOp",EDGE,"E30.right")])]})});
            var Q23;
            Q23=makeQuery(id+"F5.boolean.opBoolean","COPY",EDGE,{"derivedFrom":makeQuery(id+"F5.opExtrude","SWEPT_EDGE",EDGE,{"disambiguationData":[OSD([sQuery(id+"F2.wireOp",EDGE,"E18"),sQuery(id+"F4.wireOp",EDGE,"E30.bottom"),sQuery(id+"F4.wireOp",EDGE,"E30.left")])]})});
            var Q24;
            Q24=makeQuery(id+"F7.boolean.opBoolean","COPY",EDGE,{"derivedFrom":makeQuery(id+"F7.opExtrude","SWEPT_EDGE",EDGE,{"disambiguationData":[OSD([sQuery(id+"F2.wireOp",EDGE,"E22"),sQuery(id+"F2.wireOp",EDGE,"E23"),sQuery(id+"F6.wireOp",EDGE,"E32.bottom"),sQuery(id+"F6.wireOp",EDGE,"E32.right")])]})});
            var Q25;
            Q25=makeQuery(id+"F7.boolean.opBoolean","COPY",EDGE,{"derivedFrom":makeQuery(id+"F7.opExtrude","SWEPT_EDGE",EDGE,{"disambiguationData":[OSD([sQuery(id+"F2.wireOp",EDGE,"E22"),sQuery(id+"F2.wireOp",EDGE,"E23"),sQuery(id+"F6.wireOp",EDGE,"E33.bottom"),sQuery(id+"F6.wireOp",EDGE,"E33.right")])]})});
            var Q26;
            Q26=makeQuery(id+"F5.boolean.opBoolean","COPY",EDGE,{"derivedFrom":makeQuery(id+"F5.opExtrude","SWEPT_EDGE",EDGE,{"disambiguationData":[OSD([sQuery(id+"F4.wireOp",EDGE,"E31.bottom"),sQuery(id+"F4.wireOp",EDGE,"E31.right")])]})});
            var Q27;
            Q27=makeQuery(id+"F5.boolean.opBoolean","COPY",EDGE,{"derivedFrom":makeQuery(id+"F5.opExtrude","SWEPT_EDGE",EDGE,{"disambiguationData":[OSD([sQuery(id+"F2.wireOp",EDGE,"E18"),sQuery(id+"F4.wireOp",EDGE,"E31.bottom"),sQuery(id+"F4.wireOp",EDGE,"E31.left")])]})});
            var Q28;
            Q28=makeQuery(id+"F1.opExtrude","SWEPT_EDGE",EDGE,{"disambiguationData":[OSD([sQuery(id+"F0.wireOp",EDGE,"E8.trimOffspring"),sQuery(id+"F0.wireOp",EDGE,"E12")])]});
            var Q29;
            Q29=makeQuery(id+"F1.opExtrude","SWEPT_EDGE",EDGE,{"disambiguationData":[OSD([sQuery(id+"F0.wireOp",EDGE,"E3"),sQuery(id+"F0.wireOp",EDGE,"E8.trimOffspring")])]});
            fillet(context, id + "F36", {"entities" : qUnion([Q0, Q1, Q2, Q3, Q4, Q5, Q6, Q7, Q8, Q9, Q10, Q11, Q12, Q13, Q14, Q15, Q16, Q17, Q18, Q19, Q20, Q21, Q22, Q23, Q24, Q25, Q26, Q27, Q28, Q29]), "radius" : 0.1 * mm, "tangentPropagation" : true, "allowEdgeOverflow" : false});
        }
    });
